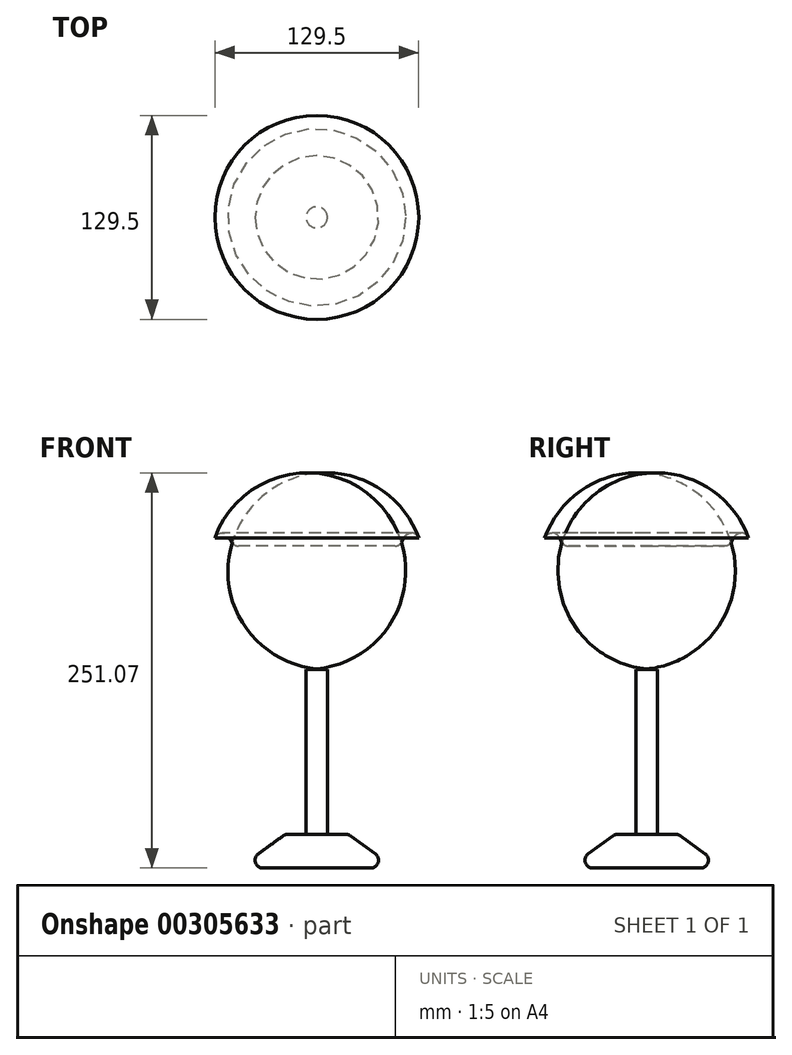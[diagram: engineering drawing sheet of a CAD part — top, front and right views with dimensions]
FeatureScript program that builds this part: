
annotation { "Feature Type Name" : "Feature", "Feature Type Description" : "" }
export const myFeature = defineFeature(function(context is Context, id is Id, definition is map)
    precondition{}
    {
        {
            var Q0;
            Q0=qCreatedBy(makeId("Front.planeOp"),FACE);
            var sketch = newSketch(context, id + "F0", { "sketchPlane" : qUnion([Q0])});
            skLineSegment(sketch, "E0", {"start": v(0, 0) * mm, "end": v(0, 183.1) * mm});
            skLineSegment(sketch, "E1", {"start": v(0, 0) * mm, "end": v(6.75, 0) * mm});
            skLineSegment(sketch, "E2", {"start": v(6.75, 0) * mm, "end": v(6.75, 104.81) * mm});
            skArc(sketch, "E3", {"start": v(6.75, 104.81) * mm, "mid": v(60, 136) * mm, "end": v(60.42, 197.72) * mm});
            skLineSegment(sketch, "E4", {"start": v(60.42, 197.72) * mm, "end": v(52.54, 183.1) * mm});
            skLineSegment(sketch, "E5", {"start": v(52.54, 183.1) * mm, "end": v(0, 183.1) * mm});
            skSolve(sketch);
        }
        {
            var Q0;
            Q0 = qSketchRegion(id + "F0", true);
            var Q1;
            Q1=sQuery(id+"F0.wireOp",EDGE,"E0");
            revolve(context, id + "F1", {"entities" : qUnion([Q0]), "axis" : qUnion([Q1]), "revolveType" : RevolveType.FULL});
        }
        {
            var Q0;
            Q0=qCreatedBy(makeId("Front.planeOp"),FACE);
            var sketch = newSketch(context, id + "F2", { "sketchPlane" : qUnion([Q0])});
            skLineSegment(sketch, "E6", {"start": v(0, 0) * mm, "end": v(20.13, 0) * mm});
            skLineSegment(sketch, "E7", {"start": v(20.13, 0) * mm, "end": v(49.58, -21.42) * mm});
            skLineSegment(sketch, "E8", {"start": v(49.58, -21.42) * mm, "end": v(61.3, -21.42) * mm});
            skLineSegment(sketch, "E9", {"start": v(0, -21.42) * mm, "end": v(0, 0) * mm});
            skLineSegment(sketch, "E10", {"start": v(0, -21.42) * mm, "end": v(52.58, -21.42) * mm});
            skSolve(sketch);
        }
        {
            var Q0;
            Q0 = qSketchRegion(id + "F2", true);
            var Q1;
            Q1=sQuery(id+"F2.wireOp",EDGE,"E9");
            revolve(context, id + "F3", {"operationType" : NewBodyOperationType.ADD, "entities" : qUnion([Q0]), "axis" : qUnion([Q1]), "revolveType" : RevolveType.FULL});
        }
        {
            var Q0;
            Q0=makeQuery(id+"F1.opRevolve","SWEPT_EDGE",EDGE,{"disambiguationData":[OSD([sQuery(id+"F0.wireOp",EDGE,"E3"),sQuery(id+"F0.wireOp",EDGE,"E4")])]});
            var Q1;
            Q1=makeQuery(id+"F1.opRevolve","SWEPT_FACE",FACE,{"disambiguationData":[OSD([sQuery(id+"F0.wireOp",EDGE,"E5")])]});
            var Q2;
            Q2=makeQuery(id+"F3.opRevolve","SWEPT_FACE",FACE,{"disambiguationData":[OSD([sQuery(id+"F2.wireOp",EDGE,"E7")])]});
            fillet(context, id + "F4", {"entities" : qUnion([Q0, Q1, Q2]), "radius" : 5 * mm, "tangentPropagation" : true, "allowEdgeOverflow" : false});
        }
    });
